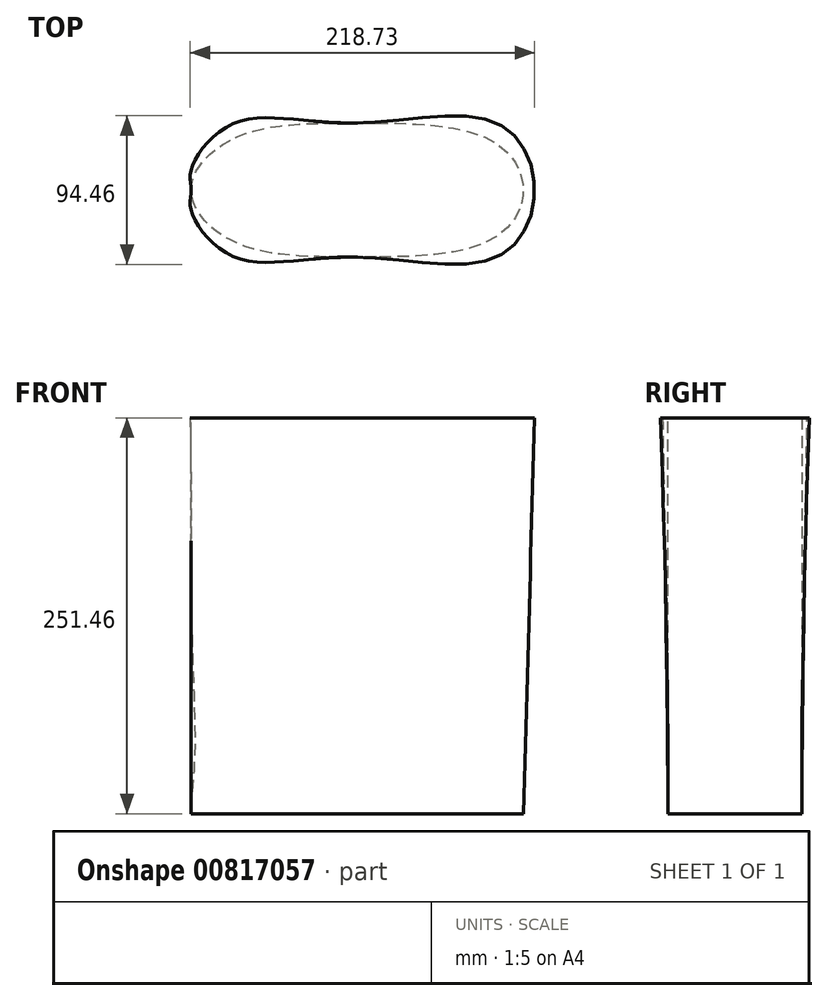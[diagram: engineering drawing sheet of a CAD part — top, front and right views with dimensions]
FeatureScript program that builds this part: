
annotation { "Feature Type Name" : "Feature", "Feature Type Description" : "" }
export const myFeature = defineFeature(function(context is Context, id is Id, definition is map)
    precondition{}
    {
        {
            var Q0;
            Q0=qCreatedBy(makeId("Top.planeOp"),FACE);
            var sketch = newSketch(context, id + "F0", { "sketchPlane" : qUnion([Q0])});
            skLineSegment(sketch, "E0", {"start": v(-93.45, 0) * mm, "end": v(117.66, 0) * mm, "construction": true});
            skLineSegment(sketch, "E1", {"start": v(-66.82, 32.6) * mm, "end": v(-66.82, -32.6) * mm, "construction": true});
            skLineSegment(sketch, "E2", {"start": v(9.26, 42.58) * mm, "end": v(9.26, -42.58) * mm, "construction": true});
            skLineSegment(sketch, "E3", {"start": v(97.22, 31.64) * mm, "end": v(97.22, -31.64) * mm, "construction": true});
            skFitSpline(sketch, "E4", {"points": [v(-93.45, 0) * mm, v(-66.82, 32.6) * mm, v(9.26, 42.58) * mm, v(97.22, 31.64) * mm, v(117.66, 0) * mm, v(97.22, -31.64) * mm, v(9.26, -42.58) * mm, v(-66.82, -32.6) * mm, v(-93.45, 0) * mm]});
            skSolve(sketch);
        }
        {
            var Q0;
            Q0=qCreatedBy(makeId("Top.planeOp"),FACE);
            cPlane(context, id + "F1", {"entities" : qUnion([Q0]), "cplaneType" : CPlaneType.OFFSET, "offset" : 251.46 * mm, "width" : 152.4 * mm, "height" : 152.4 * mm});
        }
        {
            var Q0;
            Q0=qCreatedBy(id+"F1.planeOp",FACE);
            var sketch = newSketch(context, id + "F2", { "sketchPlane" : qUnion([Q0])});
            skFitSpline(sketch, "E5.0.0", {"points": [v(-93.45, 0) * mm, v(-93.45, -12.65) * mm, v(-66.06, -42.4) * mm, v(7.93, -42.52) * mm, v(99.85, -42.98) * mm, v(124.7, 0) * mm, v(99.85, 42.98) * mm, v(7.93, 42.52) * mm, v(-66.06, 42.4) * mm, v(-93.45, 12.65) * mm, v(-93.45, 0) * mm]});
            skSolve(sketch);
        }
        {
            var Q0;
            Q0=makeQuery(id+"F0.imprint","IMPRINT",FACE,{"disambiguationData":[TD([[makeQuery(id+"F0.imprint","IMPRINT",EDGE,{"derivedFrom":sQuery(id+"F0.wireOp",EDGE,"E4")}),-1.0]])]});
            var Q1;
            Q1=makeQuery(id+"F2.imprint","IMPRINT",FACE,{"disambiguationData":[TD([[makeQuery(id+"F2.imprint","IMPRINT",EDGE,{"derivedFrom":sQuery(id+"F2.wireOp",EDGE,"E5.0.0")}),1.0]])]});
            loft(context, id + "F3", {"sheetProfilesArray" : [{ "sheetProfileEntities" : qUnion([Q0]) }, { "sheetProfileEntities" : qUnion([Q1]) }]});
        }
        {
            var Q0;
            Q0=qCreatedBy(makeId("Top.planeOp"),FACE);
            cPlane(context, id + "F4", {"entities" : qUnion([Q0]), "cplaneType" : CPlaneType.OFFSET, "offset" : 117.35 * mm, "width" : 152.4 * mm, "height" : 152.4 * mm});
        }
        {
            var Q0;
            Q0=qCreatedBy(id+"F4.planeOp",FACE);
            var sketch = newSketch(context, id + "F5", { "sketchPlane" : qUnion([Q0])});
            skLineSegment(sketch, "E6", {"start": v(-92.91, 0) * mm, "end": v(136.32, 0) * mm, "construction": true});
            skFitSpline(sketch, "E7", {"points": [v(3.82, 58.23) * mm, v(-12.58, 41.83) * mm, v(-34.35, 35.6) * mm, v(-63.75, 25.71) * mm, v(-73.37, 13.27) * mm, v(-74.78, 0) * mm, v(-73.37, -12.45) * mm, v(-63.75, -25.74) * mm, v(-28.41, -36.49) * mm, v(-6.36, -42.7) * mm, v(4.1, -64.76) * mm], "startDerivative": vector(-146.05, -180.27) * mm, "endDerivative": vector(73.04, -242.06) * mm});
            skSolve(sketch);
        }
        {
            var Q0;
            Q0=qCreatedBy(id+"F4.planeOp",FACE);
            cPlane(context, id + "F6", {"entities" : qUnion([Q0]), "cplaneType" : CPlaneType.OFFSET, "offset" : 38.1 * mm, "width" : 152.4 * mm, "height" : 152.4 * mm});
        }
        {
            var Q0;
            Q0=qCreatedBy(id+"F4.planeOp",FACE);
            cPlane(context, id + "F7", {"entities" : qUnion([Q0]), "cplaneType" : CPlaneType.OFFSET, "offset" : 38.1 * mm, "oppositeDirection" : true, "width" : 152.4 * mm, "height" : 152.4 * mm});
        }
    });
